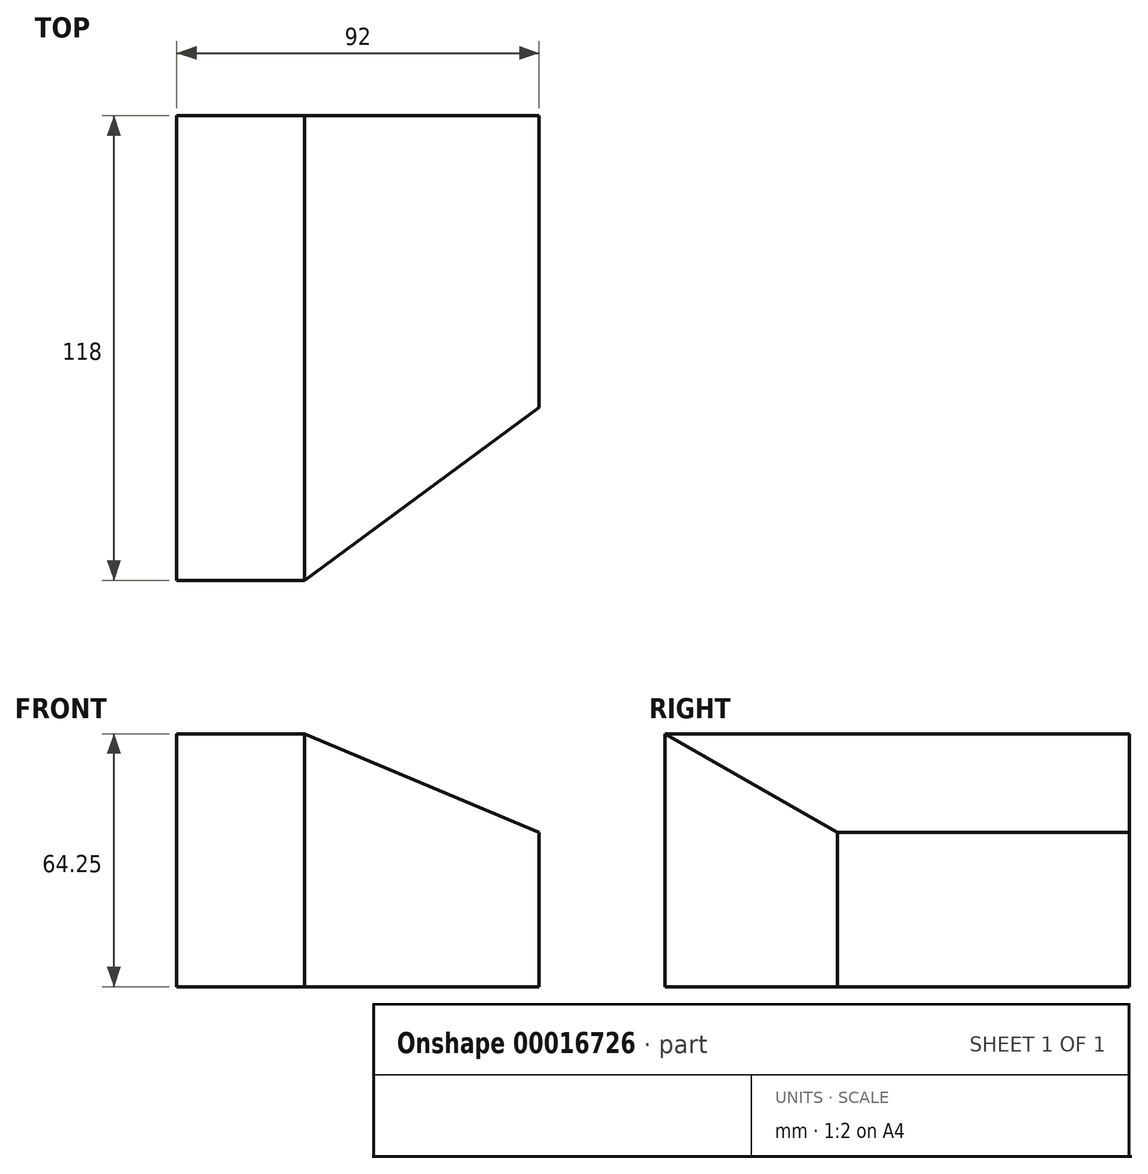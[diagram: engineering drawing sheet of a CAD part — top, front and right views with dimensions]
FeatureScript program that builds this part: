
annotation { "Feature Type Name" : "Feature", "Feature Type Description" : "" }
export const myFeature = defineFeature(function(context is Context, id is Id, definition is map)
    precondition{}
    {
        {
            var Q0;
            Q0=qCreatedBy(makeId("Top.planeOp"),FACE);
            var sketch = newSketch(context, id + "F0", { "sketchPlane" : qUnion([Q0])});
            skLineSegment(sketch, "E0", {"start": v(-23.78, 59) * mm, "end": v(-23.78, -59) * mm});
            skLineSegment(sketch, "E1", {"start": v(-23.78, -59) * mm, "end": v(8.72, -59) * mm});
            skLineSegment(sketch, "E2", {"start": v(8.72, -59) * mm, "end": v(68.22, -15.12) * mm});
            skLineSegment(sketch, "E3", {"start": v(68.22, -15.13) * mm, "end": v(68.22, 15.13) * mm});
            skLineSegment(sketch, "E4", {"start": v(68.22, 15.12) * mm, "end": v(8.72, 59) * mm, "construction": true});
            skLineSegment(sketch, "E5", {"start": v(8.72, 59) * mm, "end": v(-23.78, 59) * mm});
            skPoint(sketch, "E6", {"position": v(-23.78, 0) * mm});
            skLineSegment(sketch, "E7", {"start": v(8.72, 59) * mm, "end": v(68.22, 59) * mm});
            skLineSegment(sketch, "E8", {"start": v(68.22, 59) * mm, "end": v(68.22, 15.13) * mm});
            skSolve(sketch);
        }
        {
            var Q0;
            Q0=makeQuery(id+"F0.imprint","IMPRINT",FACE,{"disambiguationData":[TD([[makeQuery(id+"F0.imprint","IMPRINT",EDGE,{"derivedFrom":sQuery(id+"F0.wireOp",EDGE,"E0")}),1.0]])]});
            extrude(context, id + "F1", {"entities" : qUnion([Q0]), "depth" : 64.25 * mm});
        }
        {
            var Q0;
            Q0=makeQuery(id+"F1.opExtrude","CAP_EDGE",EDGE,{"disambiguationData":[OSD([sQuery(id+"F0.wireOp",EDGE,"E3")])],"isStart":false});
            chamfer(context, id + "F2", {"entities" : qUnion([Q0]), "chamferType" : ChamferType.TWO_OFFSETS, "width1" : 25 * mm, "oppositeDirection" : true, "width2" : 59.5 * mm, "tangentPropagation" : true});
        }
    });
